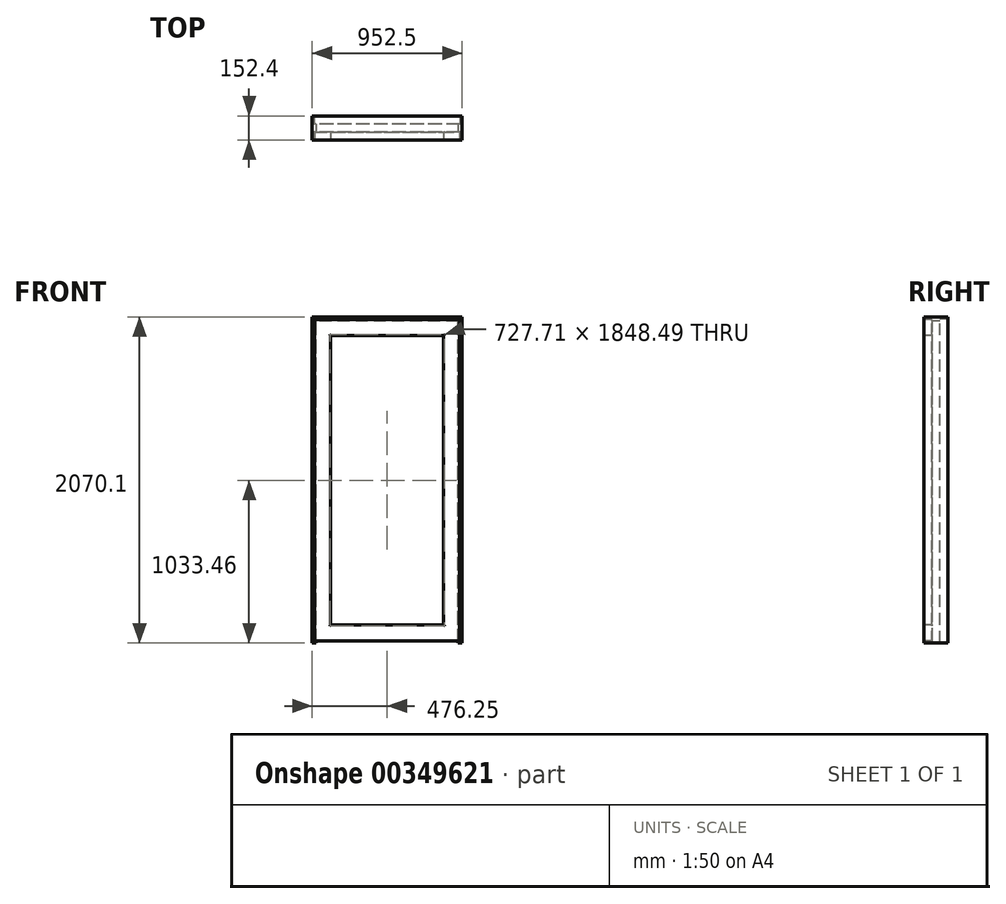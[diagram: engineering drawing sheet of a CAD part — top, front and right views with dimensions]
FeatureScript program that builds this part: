
annotation { "Feature Type Name" : "Feature", "Feature Type Description" : "" }
export const myFeature = defineFeature(function(context is Context, id is Id, definition is map)
    precondition{}
    {
        {
            var Q0;
            Q0=qCreatedBy(makeId("Front.planeOp"),FACE);
            var sketch = newSketch(context, id + "F0", { "sketchPlane" : qUnion([Q0])});
            skLineSegment(sketch, "E0.top", {"start": v(476.25, 1035.05) * mm, "end": v(-476.25, 1035.05) * mm});
            skLineSegment(sketch, "E0.left", {"start": v(476.25, -1035.05) * mm, "end": v(476.25, 1035.05) * mm});
            skLineSegment(sketch, "E0.right", {"start": v(-476.25, -1035.05) * mm, "end": v(-476.25, 1035.05) * mm});
            skPoint(sketch, "E0.middle", {"position": v(0, 0) * mm});
            skLineSegment(sketch, "E1.0", {"start": v(-463.55, -1035.05) * mm, "end": v(-463.55, 1022.35) * mm});
            skLineSegment(sketch, "E1.1", {"start": v(463.55, 1022.35) * mm, "end": v(-463.55, 1022.35) * mm});
            skLineSegment(sketch, "E1.2", {"start": v(463.55, -1035.05) * mm, "end": v(463.55, 1022.35) * mm});
            skLineSegment(sketch, "E2", {"start": v(-476.25, -1035.05) * mm, "end": v(-463.55, -1035.05) * mm});
            skLineSegment(sketch, "E3", {"start": v(463.55, -1035.05) * mm, "end": v(476.25, -1035.05) * mm});
            skSolve(sketch);
        }
        {
            var Q0;
            Q0 = qSketchRegion(id + "F0", true);
            extrude(context, id + "F1", {"entities" : qUnion([Q0]), "oppositeDirection" : true, "depth" : 152.4 * mm});
        }
        {
            var Q0;
            Q0=makeQuery(id+"F1.opExtrude","CAP_FACE",FACE,{"disambiguationData":[OSD([sQuery(id+"F0.wireOp",EDGE,"E0.top"),sQuery(id+"F0.wireOp",EDGE,"E0.left"),sQuery(id+"F0.wireOp",EDGE,"E0.right"),sQuery(id+"F0.wireOp",EDGE,"E1.0"),sQuery(id+"F0.wireOp",EDGE,"E1.1"),sQuery(id+"F0.wireOp",EDGE,"E1.2"),sQuery(id+"F0.wireOp",EDGE,"E2"),sQuery(id+"F0.wireOp",EDGE,"E3")])],"isStart":true});
            cPlane(context, id + "F2", {"entities" : qUnion([Q0]), "cplaneType" : CPlaneType.OFFSET, "offset" : 50.8 * mm, "oppositeDirection" : true, "width" : 152.4 * mm, "height" : 152.4 * mm});
        }
        {
            var Q0;
            Q0=qCreatedBy(id+"F2.planeOp",FACE);
            var sketch = newSketch(context, id + "F3", { "sketchPlane" : qUnion([Q0])});
            skLineSegment(sketch, "E4.top", {"start": v(463.55, 1022.35) * mm, "end": v(-463.55, 1022.35) * mm});
            skLineSegment(sketch, "E4.left", {"start": v(463.55, -1035.05) * mm, "end": v(463.55, 1022.35) * mm});
            skLineSegment(sketch, "E4.right", {"start": v(-463.55, -1035.05) * mm, "end": v(-463.55, 1022.35) * mm});
            skPoint(sketch, "E4.middle", {"position": v(0, 0) * mm});
            skLineSegment(sketch, "E5.0", {"start": v(450.85, -1035.05) * mm, "end": v(450.85, 1009.65) * mm});
            skLineSegment(sketch, "E5.1", {"start": v(450.85, 1009.65) * mm, "end": v(-450.85, 1009.65) * mm});
            skLineSegment(sketch, "E5.2", {"start": v(-450.85, -1035.05) * mm, "end": v(-450.85, 1009.65) * mm});
            skLineSegment(sketch, "E6", {"start": v(-450.85, -1035.05) * mm, "end": v(-463.55, -1035.05) * mm});
            skLineSegment(sketch, "E7", {"start": v(463.55, -1035.05) * mm, "end": v(450.85, -1035.05) * mm});
            skSolve(sketch);
        }
        {
            var Q0;
            Q0 = qSketchRegion(id + "F3", true);
            extrude(context, id + "F4", {"entities" : qUnion([Q0]), "operationType" : NewBodyOperationType.ADD, "oppositeDirection" : true, "depth" : 50.8 * mm});
        }
        {
            var Q0;
            Q0=makeQuery(id+"F1.opExtrude","CAP_FACE",FACE,{"disambiguationData":[OSD([sQuery(id+"F0.wireOp",EDGE,"E0.top"),sQuery(id+"F0.wireOp",EDGE,"E0.left"),sQuery(id+"F0.wireOp",EDGE,"E0.right"),sQuery(id+"F0.wireOp",EDGE,"E1.0"),sQuery(id+"F0.wireOp",EDGE,"E1.1"),sQuery(id+"F0.wireOp",EDGE,"E1.2"),sQuery(id+"F0.wireOp",EDGE,"E2"),sQuery(id+"F0.wireOp",EDGE,"E3")])],"isStart":true});
            var sketch = newSketch(context, id + "F5", { "sketchPlane" : qUnion([Q0])});
            skLineSegment(sketch, "E8.bottom", {"start": v(-460.38, 1019.18) * mm, "end": v(460.38, 1019.18) * mm});
            skLineSegment(sketch, "E8.top", {"start": v(-460.38, -1022.35) * mm, "end": v(460.38, -1022.35) * mm});
            skLineSegment(sketch, "E8.left", {"start": v(-460.38, 1019.18) * mm, "end": v(-460.37, -1022.35) * mm});
            skLineSegment(sketch, "E8.right", {"start": v(460.37, 1019.18) * mm, "end": v(460.38, -1022.35) * mm});
            skLineSegment(sketch, "E9.0", {"start": v(-358.78, -920.75) * mm, "end": v(358.78, -920.75) * mm});
            skLineSegment(sketch, "E9.1", {"start": v(-358.78, 917.58) * mm, "end": v(-358.78, -920.75) * mm});
            skLineSegment(sketch, "E9.2", {"start": v(-358.78, 917.58) * mm, "end": v(358.78, 917.58) * mm});
            skLineSegment(sketch, "E9.3", {"start": v(358.78, 917.58) * mm, "end": v(358.78, -920.75) * mm});
            skSolve(sketch);
        }
        {
            var Q0;
            Q0 = qSketchRegion(id + "F5", true);
            extrude(context, id + "F6", {"entities" : qUnion([Q0]), "oppositeDirection" : true, "depth" : 50.8 * mm});
        }
        {
            var Q0;
            Q0=makeQuery(id+"F6.opExtrude","CAP_FACE",FACE,{"disambiguationData":[OSD([sQuery(id+"F5.wireOp",EDGE,"E8.bottom"),sQuery(id+"F5.wireOp",EDGE,"E8.top"),sQuery(id+"F5.wireOp",EDGE,"E8.left"),sQuery(id+"F5.wireOp",EDGE,"E8.right"),sQuery(id+"F5.wireOp",EDGE,"E9.0"),sQuery(id+"F5.wireOp",EDGE,"E9.1"),sQuery(id+"F5.wireOp",EDGE,"E9.2"),sQuery(id+"F5.wireOp",EDGE,"E9.3")])],"isStart":true});
            var Q1;
            Q1=makeQuery(id+"F6.opExtrude","CAP_FACE",FACE,{"disambiguationData":[OSD([sQuery(id+"F5.wireOp",EDGE,"E8.bottom"),sQuery(id+"F5.wireOp",EDGE,"E8.top"),sQuery(id+"F5.wireOp",EDGE,"E8.left"),sQuery(id+"F5.wireOp",EDGE,"E8.right"),sQuery(id+"F5.wireOp",EDGE,"E9.0"),sQuery(id+"F5.wireOp",EDGE,"E9.1"),sQuery(id+"F5.wireOp",EDGE,"E9.2"),sQuery(id+"F5.wireOp",EDGE,"E9.3")])],"isStart":false});
            fillet(context, id + "F7", {"entities" : qUnion([Q0, Q1]), "radius" : 5.08 * mm, "tangentPropagation" : true, "allowEdgeOverflow" : false});
        }
    });
